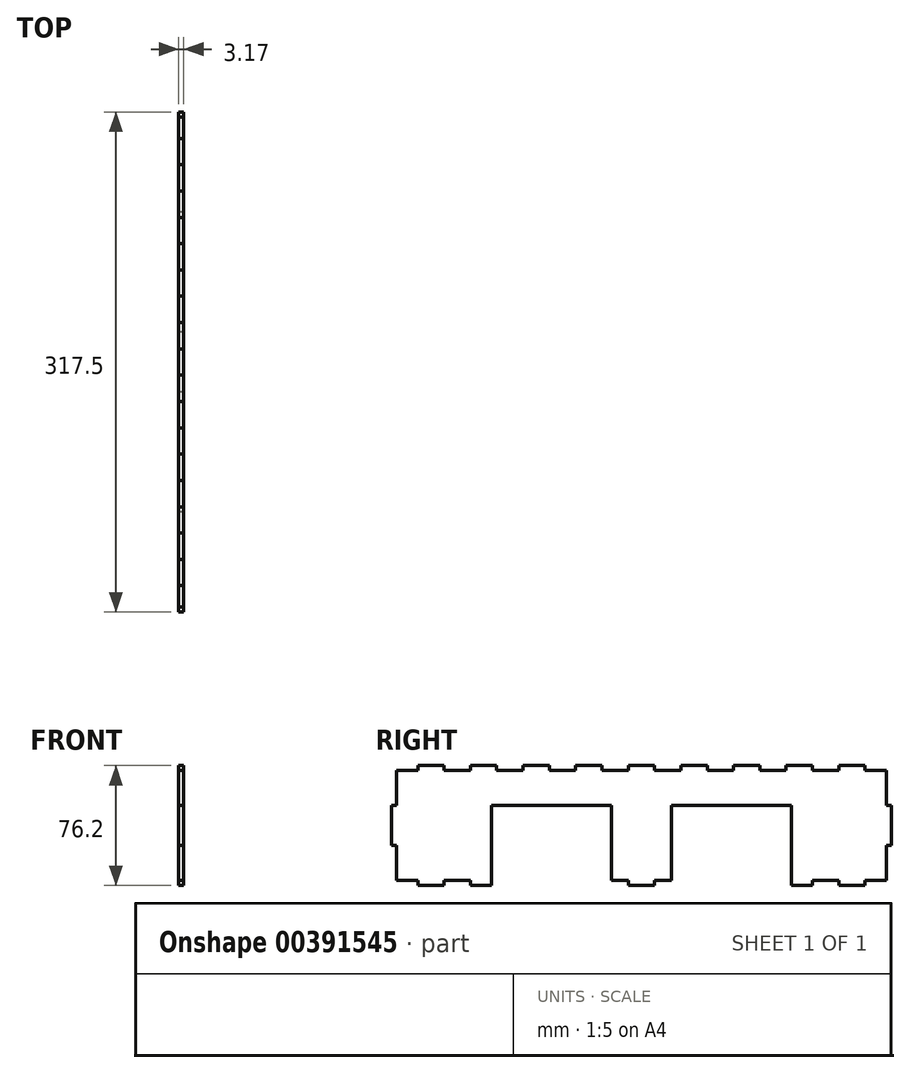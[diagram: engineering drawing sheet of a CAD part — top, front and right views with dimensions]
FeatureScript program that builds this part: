
annotation { "Feature Type Name" : "Feature", "Feature Type Description" : "" }
export const myFeature = defineFeature(function(context is Context, id is Id, definition is map)
    precondition{}
    {
        {
            var Q0;
            Q0=qCreatedBy(makeId("Right.planeOp"),FACE);
            var sketch = newSketch(context, id + "F0", { "sketchPlane" : qUnion([Q0])});
            skLineSegment(sketch, "E0.top", {"start": v(158.75, 38.1) * mm, "end": v(-158.75, 38.1) * mm, "construction": true});
            skLineSegment(sketch, "E0.left", {"start": v(158.75, -38.1) * mm, "end": v(158.75, 38.1) * mm, "construction": true});
            skLineSegment(sketch, "E0.right", {"start": v(-158.75, -38.1) * mm, "end": v(-158.75, 38.1) * mm, "construction": true});
            skPoint(sketch, "E0.middle", {"position": v(0, 0) * mm});
            skLineSegment(sketch, "E1", {"start": v(-155.57, 12.7) * mm, "end": v(-158.75, 12.7) * mm});
            skLineSegment(sketch, "E2", {"start": v(-158.75, 12.7) * mm, "end": v(-158.75, -12.7) * mm});
            skLineSegment(sketch, "E3", {"start": v(-158.75, -12.7) * mm, "end": v(-155.57, -12.7) * mm});
            skLineSegment(sketch, "E4.MirrorCS", {"start": v(155.57, 12.7) * mm, "end": v(158.75, 12.7) * mm});
            skLineSegment(sketch, "E5.MirrorCS", {"start": v(158.75, -12.7) * mm, "end": v(155.57, -12.7) * mm});
            skLineSegment(sketch, "E6.MirrorCS", {"start": v(158.75, 12.7) * mm, "end": v(158.75, -12.7) * mm});
            skLineSegment(sketch, "E7", {"start": v(-142.04, 34.93) * mm, "end": v(-142.04, 38.1) * mm});
            skLineSegment(sketch, "E8", {"start": v(-142.04, 38.1) * mm, "end": v(-125.33, 38.1) * mm});
            skLineSegment(sketch, "E9", {"start": v(-125.33, 38.1) * mm, "end": v(-125.33, 34.93) * mm});
            skLineSegment(sketch, "E10.1.0.0", {"start": v(-125.33, 34.93) * mm, "end": v(-108.62, 34.93) * mm});
            skLineSegment(sketch, "E10.1.0.1", {"start": v(-108.62, 34.93) * mm, "end": v(-108.62, 38.1) * mm});
            skLineSegment(sketch, "E10.1.0.2", {"start": v(-108.62, 38.1) * mm, "end": v(-91.9, 38.1) * mm});
            skLineSegment(sketch, "E10.1.0.3", {"start": v(-91.9, 38.1) * mm, "end": v(-91.9, 34.93) * mm});
            skLineSegment(sketch, "E10.2.0.0", {"start": v(-91.9, 34.93) * mm, "end": v(-75.2, 34.93) * mm});
            skLineSegment(sketch, "E10.2.0.1", {"start": v(-75.2, 34.93) * mm, "end": v(-75.2, 38.1) * mm});
            skLineSegment(sketch, "E10.2.0.2", {"start": v(-75.2, 38.1) * mm, "end": v(-58.49, 38.1) * mm});
            skLineSegment(sketch, "E10.2.0.3", {"start": v(-58.49, 38.1) * mm, "end": v(-58.49, 34.93) * mm});
            skLineSegment(sketch, "E10.3.0.0", {"start": v(-58.49, 34.93) * mm, "end": v(-41.78, 34.93) * mm});
            skLineSegment(sketch, "E10.3.0.1", {"start": v(-41.78, 34.93) * mm, "end": v(-41.78, 38.1) * mm});
            skLineSegment(sketch, "E10.3.0.2", {"start": v(-41.78, 38.1) * mm, "end": v(-25.07, 38.1) * mm});
            skLineSegment(sketch, "E10.3.0.3", {"start": v(-25.07, 38.1) * mm, "end": v(-25.07, 34.93) * mm});
            skLineSegment(sketch, "E10.4.0.0", {"start": v(-25.07, 34.93) * mm, "end": v(-8.36, 34.93) * mm});
            skLineSegment(sketch, "E10.4.0.1", {"start": v(-8.36, 34.93) * mm, "end": v(-8.36, 38.1) * mm});
            skLineSegment(sketch, "E10.4.0.2", {"start": v(-8.36, 38.1) * mm, "end": v(8.36, 38.1) * mm});
            skLineSegment(sketch, "E10.4.0.3", {"start": v(8.36, 38.1) * mm, "end": v(8.36, 34.93) * mm});
            skLineSegment(sketch, "E10.5.0.0", {"start": v(8.36, 34.93) * mm, "end": v(25.07, 34.93) * mm});
            skLineSegment(sketch, "E10.5.0.1", {"start": v(25.07, 34.93) * mm, "end": v(25.07, 38.1) * mm});
            skLineSegment(sketch, "E10.5.0.2", {"start": v(25.07, 38.1) * mm, "end": v(41.78, 38.1) * mm});
            skLineSegment(sketch, "E10.5.0.3", {"start": v(41.78, 38.1) * mm, "end": v(41.78, 34.93) * mm});
            skLineSegment(sketch, "E10.6.0.0", {"start": v(41.78, 34.93) * mm, "end": v(58.49, 34.93) * mm});
            skLineSegment(sketch, "E10.6.0.1", {"start": v(58.49, 34.93) * mm, "end": v(58.49, 38.1) * mm});
            skLineSegment(sketch, "E10.6.0.2", {"start": v(58.49, 38.1) * mm, "end": v(75.2, 38.1) * mm});
            skLineSegment(sketch, "E10.6.0.3", {"start": v(75.2, 38.1) * mm, "end": v(75.2, 34.93) * mm});
            skLineSegment(sketch, "E10.7.0.0", {"start": v(75.2, 34.93) * mm, "end": v(91.9, 34.93) * mm});
            skLineSegment(sketch, "E10.7.0.1", {"start": v(91.9, 34.93) * mm, "end": v(91.9, 38.1) * mm});
            skLineSegment(sketch, "E10.7.0.2", {"start": v(91.9, 38.1) * mm, "end": v(108.62, 38.1) * mm});
            skLineSegment(sketch, "E10.7.0.3", {"start": v(108.62, 38.1) * mm, "end": v(108.62, 34.93) * mm});
            skLineSegment(sketch, "E10.8.0.0", {"start": v(108.62, 34.93) * mm, "end": v(125.33, 34.93) * mm});
            skLineSegment(sketch, "E10.8.0.1", {"start": v(125.33, 34.93) * mm, "end": v(125.33, 38.1) * mm});
            skLineSegment(sketch, "E10.8.0.2", {"start": v(125.33, 38.1) * mm, "end": v(142.04, 38.1) * mm});
            skLineSegment(sketch, "E10.8.0.3", {"start": v(142.04, 38.1) * mm, "end": v(142.04, 34.93) * mm});
            skLineSegment(sketch, "E11.MirrorCS", {"start": v(-108.62, -34.93) * mm, "end": v(-108.62, -38.1) * mm});
            skLineSegment(sketch, "E12.MirrorCS", {"start": v(-142.04, -34.93) * mm, "end": v(-142.04, -38.1) * mm});
            skLineSegment(sketch, "E13.MirrorCS", {"start": v(125.33, -34.93) * mm, "end": v(125.33, -38.1) * mm});
            skLineSegment(sketch, "E14.MirrorCS", {"start": v(-8.36, -34.93) * mm, "end": v(-8.36, -38.1) * mm});
            skLineSegment(sketch, "E15.MirrorCS", {"start": v(108.62, -38.1) * mm, "end": v(108.62, -34.93) * mm});
            skLineSegment(sketch, "E16.MirrorCS", {"start": v(-125.33, -38.1) * mm, "end": v(-125.33, -34.93) * mm});
            skLineSegment(sketch, "E17.MirrorCS", {"start": v(142.04, -38.1) * mm, "end": v(142.04, -34.93) * mm});
            skLineSegment(sketch, "E18.MirrorCS", {"start": v(8.36, -38.1) * mm, "end": v(8.36, -34.93) * mm});
            skLineSegment(sketch, "E19.MirrorCS", {"start": v(-125.33, -34.93) * mm, "end": v(-108.62, -34.93) * mm});
            skLineSegment(sketch, "E20.MirrorCS", {"start": v(125.33, -38.1) * mm, "end": v(142.04, -38.1) * mm});
            skLineSegment(sketch, "E21.MirrorCS", {"start": v(-8.36, -38.1) * mm, "end": v(8.36, -38.1) * mm});
            skLineSegment(sketch, "E22.MirrorCS", {"start": v(-142.04, -38.1) * mm, "end": v(-125.33, -38.1) * mm});
            skLineSegment(sketch, "E23.MirrorCS", {"start": v(108.62, -34.93) * mm, "end": v(125.33, -34.93) * mm});
            skLineSegment(sketch, "E24", {"start": v(155.57, -12.7) * mm, "end": v(155.57, -34.93) * mm});
            skLineSegment(sketch, "E25", {"start": v(142.04, -34.93) * mm, "end": v(155.57, -34.93) * mm});
            skLineSegment(sketch, "E26", {"start": v(142.04, 34.93) * mm, "end": v(155.57, 34.93) * mm});
            skLineSegment(sketch, "E27", {"start": v(155.57, 12.7) * mm, "end": v(155.57, 34.93) * mm});
            skLineSegment(sketch, "E28", {"start": v(-142.04, -34.93) * mm, "end": v(-155.57, -34.93) * mm});
            skLineSegment(sketch, "E29", {"start": v(-155.57, -34.93) * mm, "end": v(-155.57, -12.7) * mm});
            skLineSegment(sketch, "E30", {"start": v(-142.04, 34.93) * mm, "end": v(-155.57, 34.93) * mm});
            skLineSegment(sketch, "E31", {"start": v(-155.57, 34.93) * mm, "end": v(-155.57, 12.7) * mm});
            skLineSegment(sketch, "E32.left", {"start": v(95.25, -38.1) * mm, "end": v(95.25, 12.7) * mm});
            skLineSegment(sketch, "E32.right", {"start": v(-95.25, -38.1) * mm, "end": v(-95.25, 12.7) * mm});
            skPoint(sketch, "E32.middle", {"position": v(0, -12.7) * mm});
            skLineSegment(sketch, "E33", {"start": v(-95.25, 12.7) * mm, "end": v(-19.05, 12.7) * mm});
            skLineSegment(sketch, "E34", {"start": v(19.05, 12.7) * mm, "end": v(95.25, 12.7) * mm});
            skLineSegment(sketch, "E35", {"start": v(-19.05, 12.7) * mm, "end": v(-19.05, -34.93) * mm});
            skLineSegment(sketch, "E36", {"start": v(19.05, 12.7) * mm, "end": v(19.05, -34.93) * mm});
            skLineSegment(sketch, "E37", {"start": v(-108.62, -38.1) * mm, "end": v(-95.25, -38.1) * mm});
            skLineSegment(sketch, "E38", {"start": v(-19.05, -34.93) * mm, "end": v(-8.36, -34.93) * mm});
            skLineSegment(sketch, "E39", {"start": v(8.36, -34.93) * mm, "end": v(19.05, -34.93) * mm});
            skLineSegment(sketch, "E40", {"start": v(95.25, -38.1) * mm, "end": v(108.62, -38.1) * mm});
            skSolve(sketch);
        }
        {
            var Q0;
            Q0 = qSketchRegion(id + "F0", true);
            extrude(context, id + "F1", {"entities" : qUnion([Q0]), "depth" : 3.17 * mm});
        }
    });
